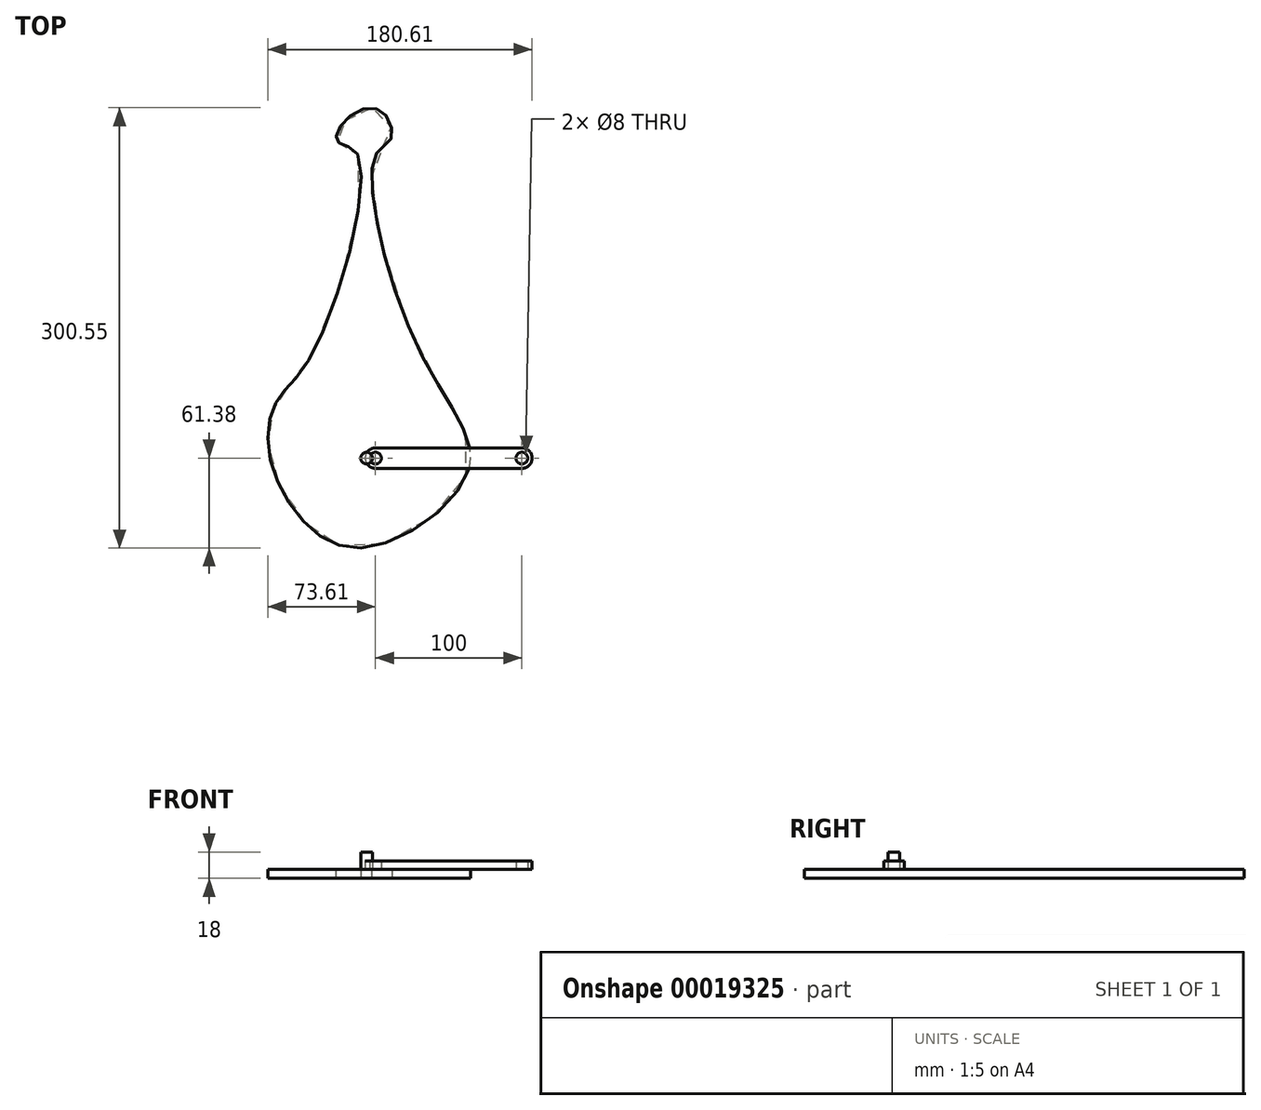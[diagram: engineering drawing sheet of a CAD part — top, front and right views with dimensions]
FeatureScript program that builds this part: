
annotation { "Feature Type Name" : "Feature", "Feature Type Description" : "" }
export const myFeature = defineFeature(function(context is Context, id is Id, definition is map)
    precondition{}
    {
        {
            var Q0;
            Q0=qCreatedBy(makeId("Top.planeOp"),FACE);
            var sketch = newSketch(context, id + "F0", { "sketchPlane" : qUnion([Q0])});
            skCircle(sketch, "E0", {"center": v(-6, 60) * mm, "radius": 4 * mm});
            skSolve(sketch);
        }
        {
            var Q0;
            Q0=qCreatedBy(makeId("Top.planeOp"),FACE);
            var sketch = newSketch(context, id + "F1", { "sketchPlane" : qUnion([Q0])});
            skLineSegment(sketch, "E1", {"start": v(0, 53) * mm, "end": v(100, 53) * mm});
            skArc(sketch, "E2", {"start": v(100, 53) * mm, "mid": v(107, 60) * mm, "end": v(100, 67) * mm});
            skLineSegment(sketch, "E3", {"start": v(100, 67) * mm, "end": v(0, 67) * mm});
            skArc(sketch, "E4", {"start": v(0, 67) * mm, "mid": v(-7, 60) * mm, "end": v(0, 53) * mm});
            skCircle(sketch, "E5", {"center": v(0, 60) * mm, "radius": 4 * mm});
            skCircle(sketch, "E6", {"center": v(100, 60) * mm, "radius": 4 * mm});
            skSolve(sketch);
        }
        {
            var Q0;
            Q0=qCreatedBy(makeId("Top.planeOp"),FACE);
            var sketch = newSketch(context, id + "F2", { "sketchPlane" : qUnion([Q0])});
            skFitSpline(sketch, "E7", {"points": [v(-12.27, 267.58) * mm, v(-42.37, 132.53) * mm, v(-66.62, 100.2) * mm, v(-72.98, 64.87) * mm, v(-46.82, 14.47) * mm, v(0, 0) * mm, v(63.82, 52.7) * mm, v(30.72, 132.2) * mm, v(0, 266.92) * mm, v(10.92, 278.46) * mm, v(2.74, 297.86) * mm, v(-21.14, 290.1) * mm, v(-25.87, 276.02) * mm, v(-12.27, 267.58) * mm]});
            skSolve(sketch);
        }
        {
            var Q0;
            Q0=makeQuery(id+"F2.imprint","IMPRINT",FACE,{"disambiguationData":[TD([[makeQuery(id+"F2.imprint","IMPRINT",EDGE,{"derivedFrom":sQuery(id+"F2.wireOp",EDGE,"E7")}),1.0]])]});
            extrude(context, id + "F3", {"entities" : qUnion([Q0]), "oppositeDirection" : true, "depth" : 6 * mm});
        }
        {
            var Q0;
            Q0=qSketchRegion(id+"F0",true);
            extrude(context, id + "F4", {"entities" : qUnion([Q0]), "operationType" : NewBodyOperationType.ADD, "depth" : 12 * mm});
        }
        {
            var Q0;
            Q0=qSketchRegion(id+"F1",true);
            extrude(context, id + "F5", {"entities" : qUnion([Q0]), "depth" : 6 * mm});
        }
    });
